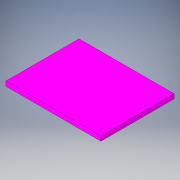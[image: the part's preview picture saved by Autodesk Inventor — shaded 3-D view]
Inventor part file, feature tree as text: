
AUTODESK INVENTOR PART (.ipt)
format: ipt  version: 2019 (Build 230136000, 136)  size: 102,400 bytes
history: native  units: mm
features: extrude x1, sketch x1
ambient origin geometry x8: Origin, YZ Plane, XZ Plane, XY Plane, X Axis, Y Axis, Z Axis, Center Point
bodies: Solid1 (feature_tree)
feature tree (2):
  extrude  "Extrusion1"  Depth=50.0mm
  sketch  "Sketch1"  dims[d0=65.0mm d1=50.0mm d2=3.18mm d3=0.0mm]
